# Revit family: 3-122-xx - Province
name_source: partatom
category: Luminarias
units: mm (PartAtom-declared; Revit-internal decimal feet)

## family parameters
Anfitrión = Techo
Compartido = No
Corte con vacíos al cargar = No
Cota de conector redondo = Diámetro de uso
Número OmniClass = 23.80.70.11
Origen de luz = No
Punto de cálculo de habitación = No
Siempre vertical = Sí
Tipo de pieza = Normal
Título OmniClass = Luminaries for Internal Lighting

## types (3) — shared parameters
Comentarios de vataje = 6 x 8.5 W at 120 V
Diffusers = Matte White Acrylic
Elevación por defecto = 0"
Fabricante = Oxygen Lighting and Fans
Lámpara = LED Array
Modelo = 3-122-xx / Providence Fan
Pendant height = 11"
References = Ref. 3 = 120 V / Ref. 37 = 277 V
URL = www.oxygenlighting.com
Voltage = 120 V
Voltage Input = 120 V or 277 V - 50/60 Hz

## per-type parameters (varying)
| type | Blades | Metal Finish |
| 3-122-15 / Black | 15 - Black | 15 - Black |
| 3-122-1540 / Black - Aged Brass | 15 - Black | 40 - Aged Brass |
| 3-122-640 / White - Aged Brass | 6 - White | 40 - Aged Brass |

## geometry (parser evidence)
native form markers: Sweep x18
no freeform markers — native parametric forms only
